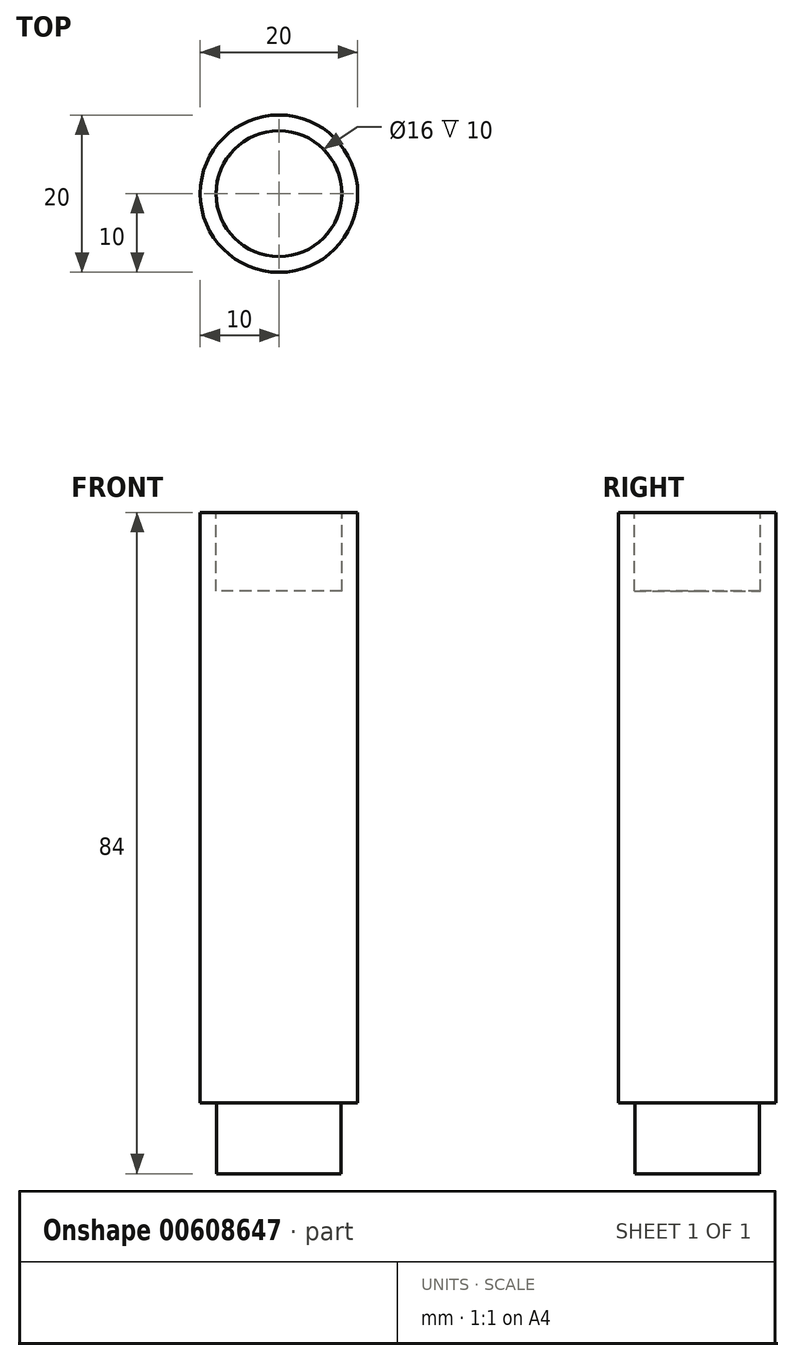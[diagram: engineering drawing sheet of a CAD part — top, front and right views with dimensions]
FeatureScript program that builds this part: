
annotation { "Feature Type Name" : "Feature", "Feature Type Description" : "" }
export const myFeature = defineFeature(function(context is Context, id is Id, definition is map)
    precondition{}
    {
        {
            var Q0;
            Q0=qCreatedBy(makeId("Top.planeOp"),FACE);
            var sketch = newSketch(context, id + "F0", { "sketchPlane" : qUnion([Q0])});
            skCircle(sketch, "E0", {"center": v(0, 0) * mm, "radius": 10 * mm});
            skCircle(sketch, "E1", {"center": v(0, 0) * mm, "radius": 7.9 * mm});
            skSolve(sketch);
        }
        {
            var Q0;
            Q0=makeQuery(id+"F0.imprint","IMPRINT",FACE,{"disambiguationData":[TD([[makeQuery(id+"F0.imprint","IMPRINT",EDGE,{"derivedFrom":sQuery(id+"F0.wireOp",EDGE,"E0")}),1.0]])]});
            var Q1;
            Q1=makeQuery(id+"F0.imprint","IMPRINT",FACE,{"disambiguationData":[TD([[makeQuery(id+"F0.imprint","IMPRINT",EDGE,{"derivedFrom":sQuery(id+"F0.wireOp",EDGE,"E1")}),1.0]])]});
            extrude(context, id + "F1", {"entities" : qUnion([Q0, Q1]), "depth" : 75 * mm, "offsetDistance" : 25 * mm});
        }
        {
            var Q0;
            Q0=makeQuery(id+"F0.imprint","IMPRINT",FACE,{"disambiguationData":[TD([[makeQuery(id+"F0.imprint","IMPRINT",EDGE,{"derivedFrom":sQuery(id+"F0.wireOp",EDGE,"E1")}),1.0]])]});
            extrude(context, id + "F2", {"entities" : qUnion([Q0]), "operationType" : NewBodyOperationType.ADD, "oppositeDirection" : true, "depth" : 9 * mm, "offsetDistance" : 25 * mm});
        }
        {
            var Q0;
            Q0=makeQuery(id+"F1.opExtrude","CAP_FACE",FACE,{"disambiguationData":[OSD([sQuery(id+"F0.wireOp",EDGE,"E0")])],"isStart":false});
            var sketch = newSketch(context, id + "F3", { "sketchPlane" : qUnion([Q0])});
            skCircle(sketch, "E2", {"center": v(0, 0) * mm, "radius": 8 * mm});
            skSolve(sketch);
        }
        {
            var Q0;
            Q0=makeQuery(id+"F3.imprint","IMPRINT",FACE,{"disambiguationData":[TD([[makeQuery(id+"F3.imprint","IMPRINT",EDGE,{"derivedFrom":sQuery(id+"F3.wireOp",EDGE,"E2")}),1.0]])]});
            extrude(context, id + "F4", {"entities" : qUnion([Q0]), "operationType" : NewBodyOperationType.REMOVE, "oppositeDirection" : true, "depth" : 10 * mm, "offsetDistance" : 25 * mm});
        }
    });
